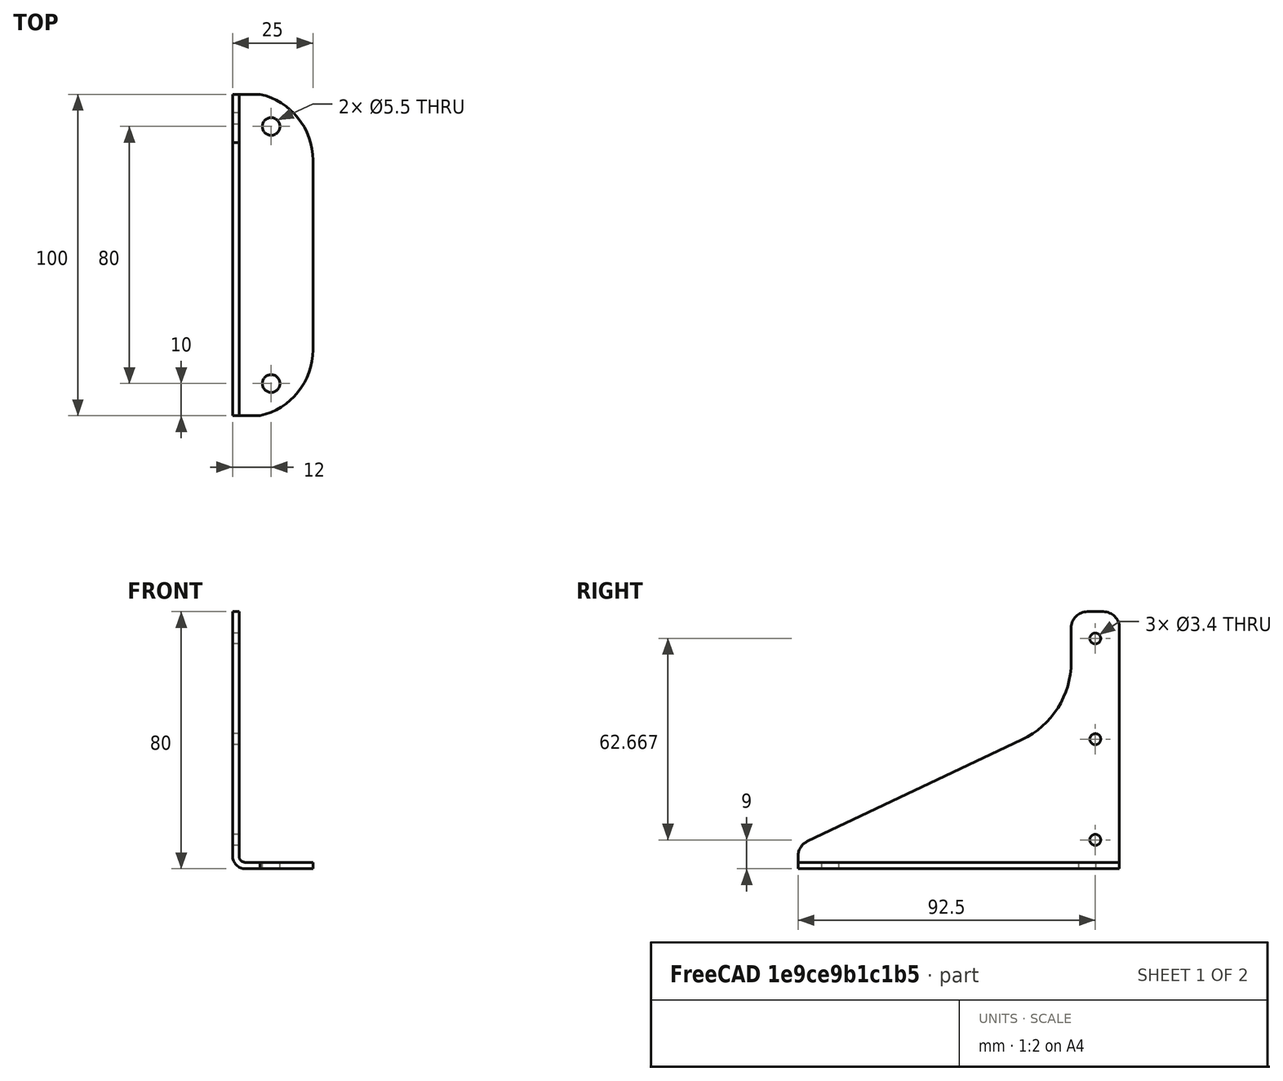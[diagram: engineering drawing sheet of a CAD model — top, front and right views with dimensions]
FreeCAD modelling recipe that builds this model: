
FCSTD DOCUMENT  (FreeCAD 1.1R38827 (Git))
Label: composit_stand3_bar_bottom_main
License: All rights reserved
LicenseURL: http://en.wikipedia.org/wiki/All_rights_reserved
objects: Part::FeaturePython×7, Sketcher::SketchObject×3, Spreadsheet::Sheet×1, Part::Feature×1, Part::Mirroring×1
note: 15 computed .brp shape members not serialized (recipe doc carries the construction recipe); baked Part::Feature solids carry a one-line shape summary decoded from their .brp

FEATURE [Part::FeaturePython] Placment  # WARN: FeaturePython — macro-defined, semantics opaque (R4)
  AttacherType = Attacher::AttachEngine3D
  ExposePlacement = true
  MarkerShape = 1
  MarkerSize = 10
  NumElements = 1
  Placement = pos=(15,40,2) rot=(0,0,1;0rad)
  Type = lattice2AttachablePlacement.AttachablePlacement
  isLattice = 1
  expr: .Placement.Base.z = <<bend_sketch>>.Constraints.thickness
FEATURE [Part::FeaturePython] Placment001  # WARN: FeaturePython — macro-defined, semantics opaque (R4)
  AttacherType = Attacher::AttachEngine3D
  ExposePlacement = true
  MarkerShape = 1
  MarkerSize = 10
  NumElements = 1
  Placement = pos=(15,-40,2) rot=(0,0,1;0rad)
  Type = lattice2AttachablePlacement.AttachablePlacement
  isLattice = 1
  expr: .Placement.Base.x = <<Placment>>.Placement.Base.x
  expr: .Placement.Base.y = -<<Placment>>.Placement.Base.y
  expr: .Placement.Base.z = <<Placment>>.Placement.Base.z
FEATURE [Part::FeaturePython] Join  label="bottom_holes_placement"  # WARN: FeaturePython — macro-defined, semantics opaque (R4)
  ExposePlacement = false
  Interleave = false
  Links = -> [Placment,Placment001]
  MarkerShape = 1
  MarkerSize = 10
  NumElements = 2
  Type = lattice2JoinArrays.JoinArrays
  isLattice = 1
FEATURE [Part::FeaturePython] Placment002  # WARN: FeaturePython — macro-defined, semantics opaque (R4)
  AttacherType = Attacher::AttachEngine3D
  ExposePlacement = true
  MarkerShape = 1
  MarkerSize = 10
  NumElements = 1
  Placement = pos=(2,42.5,9) rot=(0,1,0;1.5708rad)
  Type = lattice2AttachablePlacement.AttachablePlacement
  isLattice = 1
  expr: .Placement.Base.x = <<Properties>>.thickness
FEATURE [Part::FeaturePython] Placment003  # WARN: FeaturePython — macro-defined, semantics opaque (R4)
  AttacherType = Attacher::AttachEngine3D
  ExposePlacement = true
  MarkerShape = 1
  MarkerSize = 10
  NumElements = 1
  Placement = pos=(2,42.5,40.3333) rot=(0,1,0;1.5708rad)
  Type = lattice2AttachablePlacement.AttachablePlacement
  isLattice = 1
  expr: .Placement.Base.x = <<Properties>>.thickness
  expr: .Placement.Base.y = <<Placment002>>.Placement.Base.y
FEATURE [Part::FeaturePython] Placment004  # WARN: FeaturePython — macro-defined, semantics opaque (R4)
  AttacherType = Attacher::AttachEngine3D
  ExposePlacement = true
  MarkerShape = 1
  MarkerSize = 10
  NumElements = 1
  Placement = pos=(2,42.5,71.6667) rot=(0,1,0;1.5708rad)
  Type = lattice2AttachablePlacement.AttachablePlacement
  isLattice = 1
  expr: .Placement.Base.x = <<Properties>>.thickness
  expr: .Placement.Base.y = <<Placment002>>.Placement.Base.y
FEATURE [Part::FeaturePython] Join001  label="vert_holes_placement"  # WARN: FeaturePython — macro-defined, semantics opaque (R4)
  ExposePlacement = false
  Interleave = false
  Links = -> [Placment002,Placment003,Placment004]
  MarkerShape = 1
  MarkerSize = 10
  NumElements = 3
  Type = lattice2JoinArrays.JoinArrays
  isLattice = 1
FEATURE [Sketcher::SketchObject] Sketch  label="bend_sketch"
  ArcFitTolerance = 0
  FullyConstrained = true
  MakeInternals = false
  Placement = pos=(0,0,0) rot=(1,0,0;1.5708rad)
  expr: .Constraints.r = <<Properties>>.bend_radius
  expr: .Constraints.thickness = <<Properties>>.thickness
  sketch-geometry (4):
    g0: ArcOfCircle CenterX=4 CenterY=4 CenterZ=0 NormalX=0 NormalY=0 NormalZ=1 AngleXU=0 Radius=4 StartAngle=3.14159 EndAngle=4.71239
    g1: ArcOfCircle CenterX=4 CenterY=4 CenterZ=0 NormalX=0 NormalY=0 NormalZ=1 AngleXU=0 Radius=2 StartAngle=3.14159 EndAngle=4.71239
    g2: LineSegment StartX=4 StartY=0 StartZ=0 EndX=4 EndY=2 EndZ=0
    g3: LineSegment StartX=2.274e-11 StartY=4 StartZ=0 EndX=2 EndY=4 EndZ=0
  constraints (11):
    c: Coincident(g1,g0)
    c: Coincident(g2,g0)
    c: Coincident(g2,g1)
    c: Vertical(g2)
    c: Coincident(g3,g0)
    c: Coincident(g3,g1)
    c: Horizontal(g3)
    c: Tangent(g0,g-1) = -1.5708
    c: Tangent(g0,g-2) = 1.5708
    c: DistanceY(g2,g2) = 2  'thickness'
    c: Radius(g1) = 2  'r'
FEATURE [Spreadsheet::Sheet] Spreadsheet  label="Properties"
  cells = B2(width)==100 mm; C2(length)==25 mm; D2(height)==80 mm; E2(bend_radius)==2 mm; F2(thickness)==2 mm
FEATURE [Sketcher::SketchObject] Sketch002  label="vert_sketch"
  ArcFitTolerance = 0
  FullyConstrained = true
  MakeInternals = false
  Placement = pos=(0,0,0) rot=(0.57735,0.57735,0.57735;2.0944rad)
  expr: Constraints[11] = <<Properties>>.width
  expr: Constraints[12] = <<Properties>>.bend_radius + <<Properties>>.thickness
  expr: Constraints[19] = <<Properties>>.height
  sketch-geometry (11):
    g0: LineSegment StartX=-50 StartY=4 StartZ=0 EndX=50 EndY=4 EndZ=0
    g1: LineSegment StartX=50 StartY=4 StartZ=0 EndX=50 EndY=75 EndZ=0
    g2: LineSegment StartX=45 StartY=80 StartZ=0 EndX=40 EndY=80 EndZ=0
    g3: ArcOfCircle CenterX=-45 CenterY=4 CenterZ=0 NormalX=0 NormalY=0 NormalZ=1 AngleXU=0 Radius=5 StartAngle=2.01309 EndAngle=3.14159
    g4: ArcOfCircle CenterX=40 CenterY=75 CenterZ=0 NormalX=0 NormalY=0 NormalZ=1 AngleXU=0 Radius=5 StartAngle=1.5708 EndAngle=3.14159
    g5: ArcOfCircle CenterX=45 CenterY=75 CenterZ=0 NormalX=0 NormalY=0 NormalZ=1 AngleXU=0 Radius=5 StartAngle=-9e-16 EndAngle=1.5708
    g6: GeomPoint [constr] X=50 Y=80 Z=0
    g7: LineSegment StartX=-47.14 StartY=8.51887 StartZ=0 EndX=19.6724 EndY=40.1599 EndZ=0
    g8: ArcOfCircle CenterX=8.203 CenterY=64.3783 CenterZ=0 NormalX=0 NormalY=0 NormalZ=1 AngleXU=0 Radius=26.797 StartAngle=5.15468 EndAngle=6.28319
    g9: LineSegment StartX=35 StartY=75 StartZ=0 EndX=35 EndY=64.3783 EndZ=0
    g10: LineSegment [constr] StartX=35 StartY=64.3783 StartZ=0 EndX=35 EndY=0 EndZ=0
  constraints (28):
    c: Coincident(g0,g1)
    c: Vertical(g1)
    c: Horizontal(g2)
    c: PointOnObject(g3,g0)
    c: Coincident(g3,g0)
    c: Tangent(g2,g4) = -1.5708
    c: PointOnObject(g6,g2)
    c: PointOnObject(g6,g1)
    c: Tangent(g2,g5) = -1.5708
    c: Tangent(g1,g5) = -1.5708
    c: Symmetric(g0,g0,g-2)
    c: DistanceX(g0,g0) = 100
    c: DistanceY(g0) = 4
    c: Equal(g5,g4)
    c: Radius(g5) = 5
    c: Tangent(g8,g7) = -1.5708
    c: Tangent(g7,g3) = 1.5708
    c: PointOnObject(g10,g-1)
    c: DistanceX(g4,g1) = 15
    c: DistanceY(g6) = 80
    c: Radius(g3) = 5
    c: Coincident(g9,g10)
    c: Vertical(g9)
    c: Vertical(g10)
    c: Tangent(g8,g9) = 1.5708
    c: Radius(g8) = 26.797
    c: Tangent(g9,g4) = -1.5708
    c: Angle(g7) = 0.442289
FEATURE [Part::Feature] Body163  label="pillar_bottom_material_0.30ansi002"
  Placement = pos=(0,0,0) rot=(0,0,1;1.5708rad)
  shape: bbox 25 x 100 x 80 mm, 23 faces (baked)
FEATURE [Part::Mirroring] Part__Mirroring  label="pillar_bottom_material_0.30ansi002 (Mirror #1)"
  Base = (0,0,0)
  Normal = (0,1,0)
  Source = -> Body163
FEATURE [Sketcher::SketchObject] Sketch001  label="bottom_sketch"
  ArcFitTolerance = 0
  ExternalGeometry = -> [Part__Mirroring]
  FullyConstrained = true
  MakeInternals = false
  expr: Constraints[4] = <<Properties>>.width
  expr: Constraints[5] = <<Properties>>.length
  expr: Constraints[6] = <<Properties>>.bend_radius + <<Properties>>.thickness
  sketch-geometry (6):
    g0: LineSegment StartX=4 StartY=50 StartZ=0 EndX=4 EndY=-50 EndZ=0
    g1: LineSegment StartX=25 StartY=-29 StartZ=0 EndX=25 EndY=29 EndZ=0
    g2: GeomPoint [constr] X=14.5 Y=0 Z=0
    g3: GeomPoint [constr] X=25 Y=50 Z=0
    g4: ArcOfCircle CenterX=4 CenterY=29 CenterZ=0 NormalX=0 NormalY=0 NormalZ=1 AngleXU=0 Radius=21 StartAngle=1e-16 EndAngle=1.5708
    g5: ArcOfCircle CenterX=4 CenterY=-29 CenterZ=0 NormalX=0 NormalY=0 NormalZ=1 AngleXU=0 Radius=21 StartAngle=4.71239 EndAngle=6.28319
  constraints (16):
    c: Vertical(g0)
    c: Vertical(g1)
    c: Symmetric(g0,g3,g2)
    c: PointOnObject(g2,g-1)
    c: DistanceY(g0,g3) = 100
    c: DistanceX(g3) = 25
    c: DistanceX(g0) = 4
    c: PointOnObject(g3,g1)
    c: Tangent(g4,g1) = -1.5708
    c: Radius(g4) = 21
    c: Coincident(g4,g0)
    c: PointOnObject(g4,g0)
    c: Horizontal(g0,g3)
    c: PointOnObject(g5,g0)
    c: Coincident(g5,g0)
    c: Tangent(g5,g1) = -1.5708
